# Revit family: Deca_Assento poliéster slow close com Protekto_Carrara.Lk.Nuova.Level_AP.237
name_source: partatom
category: Plumbing Fixtures
units: mm (PartAtom-declared; Revit-internal decimal feet)

## family parameters
Cut with Voids When Loaded = No
Host = Face
Part Type = Normal
Room Calculation Point = No
Round Connector Dimension = Use Diameter
Shared = No

## types (27) — shared parameters
Acompanha o Produto = FIXAÇÃO ASSENTO  (FERRAGEM C/AMORTECEDOR )
Aprovado por = quattroD
Atendimento ao Cliente = 0800-0117073
Categoria = ASSENTOS
Composição Anel Vedação = -
Composição Assento = -
Composição Básica = Resina Poliéster
Composição Componente = Não Possui
Consumo = -
Cor Interna = -
Cor Secundária = -
Criado por = quattroD
Código Pai = AP.237
Description = Assento poliéster slow close com Protekto
Informações Complementares = -
Itens de Instalação = -
Linha = Assento Poliéster Luxo
Manufacturer = Deca
Norma = NBR-16729
Pressão máx. funcionamento = -
Pressão mín. Aquec. Acúmulo = -
Pressão mín. Aquec. Passagem = -
Pressão mín. funcionamento = -
Saída de Esgoto = -
Segmento = Banheiro Luxo
Tipo de dispositivo economizador = -
Tipo de mecanismo utilizado = -
Tipo de rosca de entrada = -
Tipo de rosca de saída = -
URL = www.deca.com.br
Vazão na Pressão máx. (L/min) = -
Vazão na Pressão mín. (L/min) = -
zero-valued in all types: Default Elevation

## per-type parameters (varying)
| type | Cor Principal | Cores Componente | Material | Material Secundário | Model | Peso Líquido (Kg) |
| AP.237.17_Branco | Branco | Cromado | Deca_Plástico - Branco | Deca_Ligas de Cobre (Bronze e Latão) | AP.237.17 | 4.4 |
| AP.237.BL.MT.17_Branco | Branco | Black Matte | Deca_Plástico - Branco | Deca_Black Matte | AP.237.BL.MT.17 | 4.4 |
| AP.237.GL.RD.22_Marrom Fosco | Marrom fosco | Red Gold | Deca_Plástico - Marrom Fosco | Deca_Red Gold | AP.237.GL.RD.22 | 4.4 |
| AP.237.22_Marrom Fosco | Marrom | Cromado | Deca_Plástico - Marrom Fosco | Deca_Ligas de Cobre (Bronze e Latão) | AP.237.22 | 4.4 |
| AP.237.BL.NO.86_Cinza Fosco | Cinza fosco | Black Noir | Deca_Plástico - Cinza Fosco | Deca_Black Noir | AP.237.BL.NO.86 | 4.4 |
| AP.237.86_Cinza Fosco | Cinza fosco | Cromado | Deca_Plástico - Cinza Fosco | Deca_Ligas de Cobre (Bronze e Latão) | AP.237.86 | 4.4 |
| AP.237.BL.NO.17_Branco | Branco | Black Noir | Deca_Plástico - Branco | Deca_Black Noir | AP.237.BL.NO.17 | 4.4 |
| AP.237.BL.MT.86_Cinza Fosco | Cinza fosco | Black Matte | Deca_Plástico - Cinza Fosco | Deca_Black Matte | AP.237.BL.MT.86 | 4.4 |
| AP.237.GL.MT.86_Cinza Fosco | Cinza fosco | Gold Matte | Deca_Plástico - Cinza Fosco | Deca_Gold Matte | AP.237.GL.MT.86 | 4.4 |
| AP.237.GL.RD.17_Branco | Branco | Red Gold | Deca_Plástico - Branco | Deca_Red Gold | AP.237.GL.RD.17 | 4.4 |
| AP.237.GL.RD.86_Cinza Fosco | Cinza fosco | Red Gold | Deca_Plástico - Cinza Fosco | Deca_Red Gold | AP.237.GL.RD.86 | 4.4 |
| AP.237.GL.MT.22_Marrom Fosco | Marrom fosco | Gold Matte | Deca_Plástico - Marrom Fosco | Deca_Gold Matte | AP.237.GL.MT.22 | 4.4 |
| AP.237.GL.22_Marrom Fosco | Marrom | Gold | Deca_Plástico - Marrom Fosco | Deca_Gold | AP.237.GL.22 | 4.4 |
| AP.237.GL.86_Cinza Fosco | Cinza fosco | Gold | Deca_Plástico - Cinza Fosco | Deca_Gold | AP.237.GL.86 | 4.4 |
| AP.237.GL.17_Branco | Branco | Gold | Deca_Plástico - Branco | Deca_Gold | AP.237.GL.17 | 4.4 |
| AP.237.GL.MT.17_Branco | Branco | Gold Matte | Deca_Plástico - Branco | Deca_Gold Matte | AP.237.GL.MT.17 | 4.4 |
| AP.237.CT.MT.86_Cinza Fosco | Cinza fosco | Corten | Deca_Plástico - Cinza Fosco | Deca_Corten | AP.237.CT.MT.86 | 4.4 |
| AP.237.CT.MT.22_Marrom Fosco | Marrom fosco | Corten | Deca_Plástico - Marrom Fosco | Deca_Corten | AP.237.CT.MT.22 | 4.4 |
| AP.237.CT.MT.17_Branco | Branco | Corten | Deca_Plástico - Branco | Deca_Corten | AP.237.CT.MT.17 | 4.4 |
| AP.237.CT.MT.94_Ébano Fosco | Ébano fosco | Corten | Deca_Plástico - Ébano Fosco | Deca_Corten | AP.237.CT.MT.94 | 4.4 |
| AP.237.GL.95_Ébano | Ébano | Gold | Deca_Plástico - Ébano | Deca_Gold | AP.237.GL.95 | 4.4 |
| AP.237.BL.NO.95_Ébano | Ébano | Black Noir | Deca_Plástico - Ébano | Deca_Black Noir | AP.237.BL.NO.95 | 4.4 |
| AP.237.BL.MT.94_Ébano Fosco | Ébano fosco | Black Matte | Deca_Plástico - Ébano Fosco | Deca_Black Matte | AP.237.BL.MT.94 | 4.4 |
| AP.237.94_Ébano Fosco | Ébano fosco | Cromado | Deca_Plástico - Ébano Fosco | Deca_Ligas de Cobre (Bronze e Latão) | AP.237.94 | 3.7 |
| AP.237.BL.NO.94_Ébano Fosco | Ébano fosco | Black Noir | Deca_Plástico - Ébano Fosco | Deca_Black Noir | AP.237.BL.NO.94 | 4.4 |
| AP.237.BL.MT.95_Ébano | Ébano | Black Matte | Deca_Plástico - Ébano | Deca_Black Matte | AP.237.BL.MT.95 | 4.4 |
| AP.237.95_Ébano | Ébano | Cromado | Deca_Plástico - Ébano | Deca_Ligas de Cobre (Bronze e Latão) | AP.237.95 | 4.4 |

## geometry (parser evidence)
native form markers: Sweep x3
no freeform markers — native parametric forms only
